# Revit family: 206_TAK-___ for MAK
name_source: partatom
category: Duct Accessories
units: mm (PartAtom-declared; Revit-internal decimal feet)

## family parameters
Always vertical = Yes
Cut with Voids When Loaded = No
Part Type = Breaks Into
Round Connector Dimension = Use Diameter
Shared = No
Work Plane-Based = No

## types (4) — shared parameters
CAT0 = Yes
Description = Balancing plenum box
H2 = 50 mm  [stored 0.164042 ft]
H2__ve = -50 mm  [stored -0.164042 ft]
L2D = 50 mm  [stored 0.164042 ft]
Manufacturer = Climecon
QmdConnectorList = 201;D;202;CLD
URL = www.climecon.fi
magiPartTypeId = 206
magiProductFamilyId = TAK-*/* for MAK
zero-valued in all types: MC_Default_elevation

## per-type parameters (varying)
| type | B2 | C | CLD | CX | D | H1 | H2D | HH | HX | L | L1 | L__ve | W2D |
| TAK-100/125 for MAK | 32 mm | 92 mm  [stored 0.301837 ft] | 125 mm | 63 mm | 100 mm | 74 mm | 100 mm  [stored 0.328084 ft] | 70 mm  [stored 0.229659 ft] | 33 mm | 450 mm  [stored 1.47638 ft] | 135 mm  [stored 0.442913 ft] | -450 mm  [stored -1.47638 ft] | 100 mm  [stored 0.328084 ft] |
| TAK-200/250 for MAK | 48 mm  [stored 0.15748 ft] | 155 mm  [stored 0.50853 ft] | 250 mm | 125 mm  [stored 0.410105 ft] | 200 mm | 143 mm  [stored 0.46916 ft] | 200 mm  [stored 0.656168 ft] | 120 mm  [stored 0.393701 ft] | 49 mm | 570 mm  [stored 1.87008 ft] | 200 mm  [stored 0.656168 ft] | -570 mm  [stored -1.87008 ft] | 200 mm  [stored 0.656168 ft] |
| TAK-160/200 for MAK | 41 mm | 130 mm  [stored 0.426509 ft] | 200 mm | 100 mm  [stored 0.328084 ft] | 160 mm | 117 mm | 160 mm  [stored 0.524934 ft] | 100 mm  [stored 0.328084 ft] | 41 mm | 500 mm  [stored 1.64042 ft] | 170 mm  [stored 0.557743 ft] | -500 mm  [stored -1.64042 ft] | 160 mm  [stored 0.524934 ft] |
| TAK-125/160 for MAK | 32 mm | 110 mm  [stored 0.360892 ft] | 160 mm | 80 mm  [stored 0.262467 ft] | 125 mm | 99 mm | 125 mm  [stored 0.410105 ft] | 83 mm | 33 mm | 450 mm  [stored 1.47638 ft] | 135 mm  [stored 0.442913 ft] | -450 mm  [stored -1.47638 ft] | 125 mm  [stored 0.410105 ft] |

note: column(s) folded — value = type name in every type: magiProductCode, magiProductId

note: [stored X ft] marks values corroborated as IEEE doubles in the binary element streams (Revit-internal decimal feet)

## geometry (parser evidence)
native form markers: Sweep x2
no freeform markers — native parametric forms only
